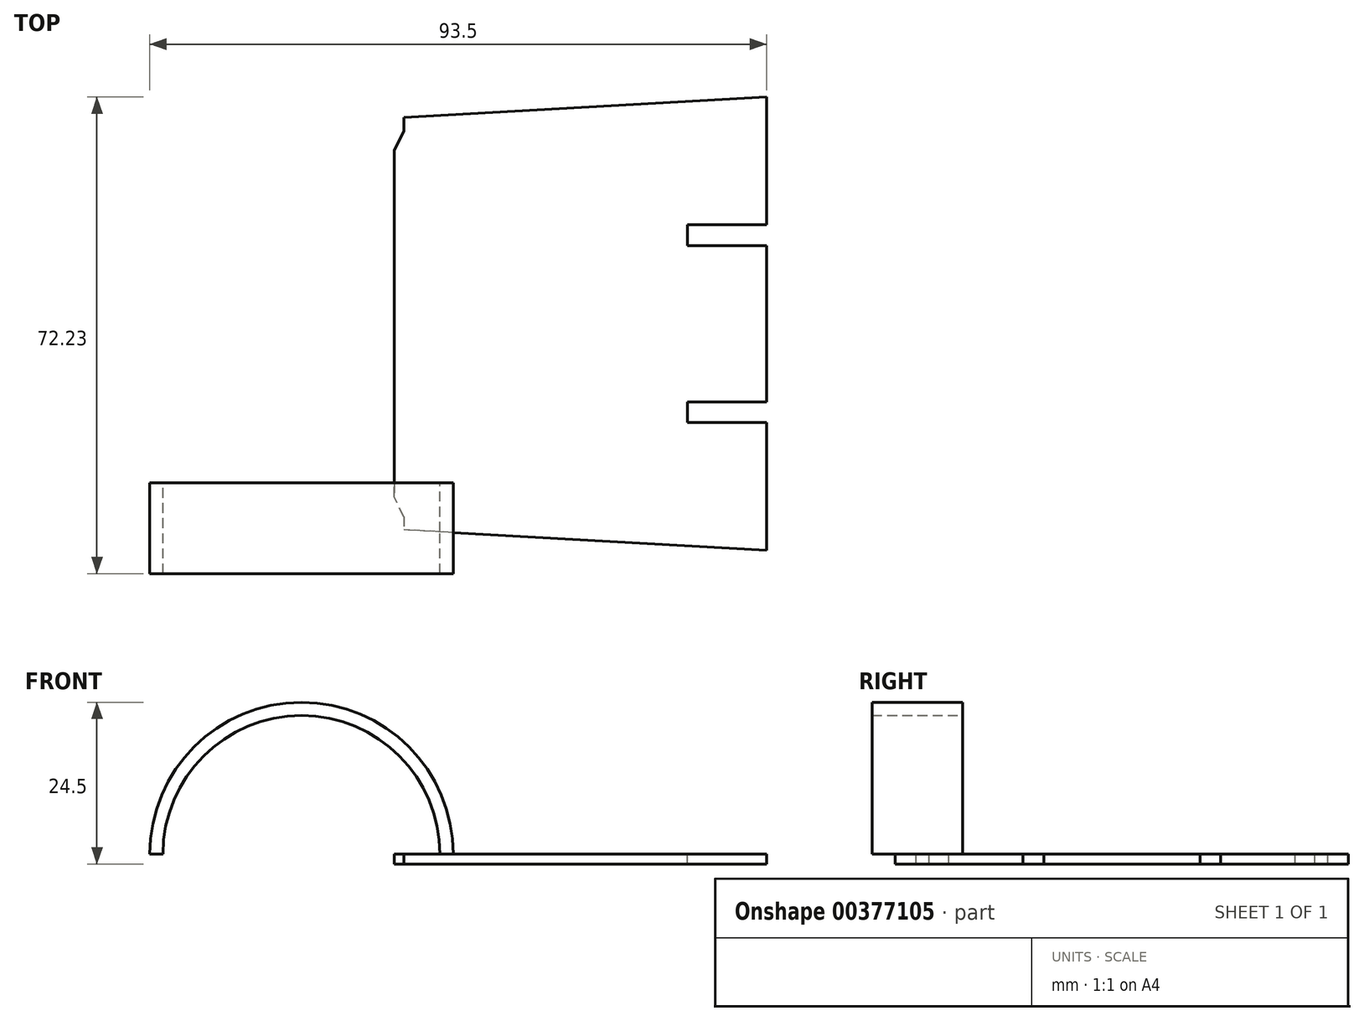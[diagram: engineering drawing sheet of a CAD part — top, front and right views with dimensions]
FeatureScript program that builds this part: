
annotation { "Feature Type Name" : "Feature", "Feature Type Description" : "" }
export const myFeature = defineFeature(function(context is Context, id is Id, definition is map)
    precondition{}
    {
        {
            var Q0;
            Q0=qCreatedBy(makeId("Top.planeOp"),FACE);
            var sketch = newSketch(context, id + "F0", { "sketchPlane" : qUnion([Q0])});
            skLineSegment(sketch, "E0", {"start": v(0, 34.35) * mm, "end": v(0, -34.35) * mm});
            skLineSegment(sketch, "E1", {"start": v(0, -34.35) * mm, "end": v(-55, -31.23) * mm});
            skLineSegment(sketch, "E2", {"start": v(0, 34.35) * mm, "end": v(-55, 31.23) * mm});
            skLineSegment(sketch, "E3", {"start": v(-55, 31.23) * mm, "end": v(-55, -31.23) * mm});
            skPoint(sketch, "E4", {"position": v(0, 0) * mm});
            skPoint(sketch, "E5", {"position": v(-55, 0) * mm});
            skSolve(sketch);
        }
        {
            var Q0;
            Q0 = qSketchRegion(id + "F0", true);
            extrude(context, id + "F1", {"entities" : qUnion([Q0]), "oppositeDirection" : true, "depth" : 1.5 * mm});
        }
        {
            var Q0;
            Q0=makeQuery(id+"F1.opExtrude","CAP_FACE",FACE,{"disambiguationData":[OSD([sQuery(id+"F0.wireOp",EDGE,"E0"),sQuery(id+"F0.wireOp",EDGE,"E1"),sQuery(id+"F0.wireOp",EDGE,"E2"),sQuery(id+"F0.wireOp",EDGE,"E3")])],"isStart":true});
            var sketch = newSketch(context, id + "F2", { "sketchPlane" : qUnion([Q0])});
            skLineSegment(sketch, "E6", {"start": v(0, 15) * mm, "end": v(0, -15) * mm, "construction": true});
            skPoint(sketch, "E7", {"position": v(0, 0) * mm});
            skLineSegment(sketch, "E8.bottom", {"start": v(0, 15) * mm, "end": v(-12, 15) * mm});
            skLineSegment(sketch, "E8.top", {"start": v(0, 11.85) * mm, "end": v(-12, 11.85) * mm});
            skLineSegment(sketch, "E8.left", {"start": v(0, 15) * mm, "end": v(0, 11.85) * mm});
            skLineSegment(sketch, "E8.right", {"start": v(-12, 15) * mm, "end": v(-12, 11.85) * mm});
            skLineSegment(sketch, "E9.bottom", {"start": v(0, -15) * mm, "end": v(-12, -15) * mm});
            skLineSegment(sketch, "E9.top", {"start": v(0, -11.85) * mm, "end": v(-12, -11.85) * mm});
            skLineSegment(sketch, "E9.left", {"start": v(0, -15) * mm, "end": v(0, -11.85) * mm});
            skLineSegment(sketch, "E9.right", {"start": v(-12, -15) * mm, "end": v(-12, -11.85) * mm});
            skSolve(sketch);
        }
        {
            var Q0;
            Q0 = qSketchRegion(id + "F2", true);
            var Q1;
            Q1=makeQuery(id+"F1.opExtrude","CAP_FACE",FACE,{"disambiguationData":[OSD([sQuery(id+"F0.wireOp",EDGE,"E0"),sQuery(id+"F0.wireOp",EDGE,"E1"),sQuery(id+"F0.wireOp",EDGE,"E2"),sQuery(id+"F0.wireOp",EDGE,"E3")])],"isStart":false});
            extrude(context, id + "F3", {"entities" : qUnion([Q0]), "operationType" : NewBodyOperationType.REMOVE, "endBound" : BoundingType.UP_TO_SURFACE, "oppositeDirection" : true, "endBoundEntityFace" : qUnion([Q1]), "depth" : 25 * mm});
        }
        {
            var Q0;
            Q0=qCreatedBy(makeId("Top.planeOp"),FACE);
            var sketch = newSketch(context, id + "F4", { "sketchPlane" : qUnion([Q0])});
            skLineSegment(sketch, "E10.0", {"start": v(-55, 29.25) * mm, "end": v(-55, -29.25) * mm});
            skLineSegment(sketch, "E11", {"start": v(-55, 29.25) * mm, "end": v(-56.45, 26.25) * mm});
            skLineSegment(sketch, "E12", {"start": v(-56.45, 26.25) * mm, "end": v(-56.45, -26.25) * mm});
            skLineSegment(sketch, "E13", {"start": v(-56.45, -26.25) * mm, "end": v(-55, -29.25) * mm});
            skPoint(sketch, "E14.orphan", {"position": v(-55, -31.23) * mm});
            skPoint(sketch, "E15.orphan", {"position": v(-55, 31.23) * mm});
            skLineSegment(sketch, "E16", {"start": v(-55, 31.23) * mm, "end": v(-55, 29.25) * mm, "construction": true});
            skLineSegment(sketch, "E17", {"start": v(-55, -29.25) * mm, "end": v(-55, -31.23) * mm, "construction": true});
            skPoint(sketch, "E18", {"position": v(-55, 0) * mm});
            skPoint(sketch, "E19", {"position": v(-56.45, 0) * mm});
            skSolve(sketch);
        }
        {
            var Q0;
            Q0 = qSketchRegion(id + "F4", true);
            var Q1;
            Q1=makeQuery(id+"F1.opExtrude","CAP_FACE",FACE,{"disambiguationData":[OSD([sQuery(id+"F0.wireOp",EDGE,"E0"),sQuery(id+"F0.wireOp",EDGE,"E1"),sQuery(id+"F0.wireOp",EDGE,"E2"),sQuery(id+"F0.wireOp",EDGE,"E3")])],"isStart":false});
            extrude(context, id + "F5", {"entities" : qUnion([Q0]), "operationType" : NewBodyOperationType.ADD, "endBound" : BoundingType.UP_TO_SURFACE, "oppositeDirection" : true, "endBoundEntityFace" : qUnion([Q1]), "depth" : 25 * mm});
        }
        {
            var Q0;
            Q0=qCreatedBy(makeId("Front.planeOp"),FACE);
            var sketch = newSketch(context, id + "F6", { "sketchPlane" : qUnion([Q0])});
            skArc(sketch, "E20", {"start": v(-49.5, 0) * mm, "mid": v(-70.5, 21) * mm, "end": v(-91.5, 0) * mm});
            skPoint(sketch, "E21", {"position": v(-49.5, 0) * mm});
            skLineSegment(sketch, "E22", {"start": v(-49.5, 0) * mm, "end": v(-91.5, 0) * mm, "construction": true});
            skArc(sketch, "E23.0", {"start": v(-47.5, 0) * mm, "mid": v(-70.5, 23) * mm, "end": v(-93.5, 0) * mm});
            skLineSegment(sketch, "E24", {"start": v(-47.5, 0) * mm, "end": v(-49.5, 0) * mm});
            skLineSegment(sketch, "E25", {"start": v(-91.5, 0) * mm, "end": v(-93.5, 0) * mm});
            skSolve(sketch);
        }
        {
            var Q0;
            Q0 = qSketchRegion(id + "F6", true);
            extrude(context, id + "F7", {"entities" : qUnion([Q0]), "operationType" : NewBodyOperationType.ADD, "endBound" : BoundingType.SYMMETRIC, "depth" : 75.75 * mm});
        }
        {
            var Q0;
            Q0=makeQuery(id+"F7.opExtrude","CAP_FACE",FACE,{"disambiguationData":[OSD([sQuery(id+"F6.wireOp",EDGE,"E20"),sQuery(id+"F6.wireOp",EDGE,"E23.0"),sQuery(id+"F6.wireOp",EDGE,"E24"),sQuery(id+"F6.wireOp",EDGE,"E25")])],"isStart":true});
            extrude(context, id + "F8", {"entities" : qUnion([Q0]), "operationType" : NewBodyOperationType.REMOVE, "oppositeDirection" : true, "depth" : 62 * mm});
        }
    });
